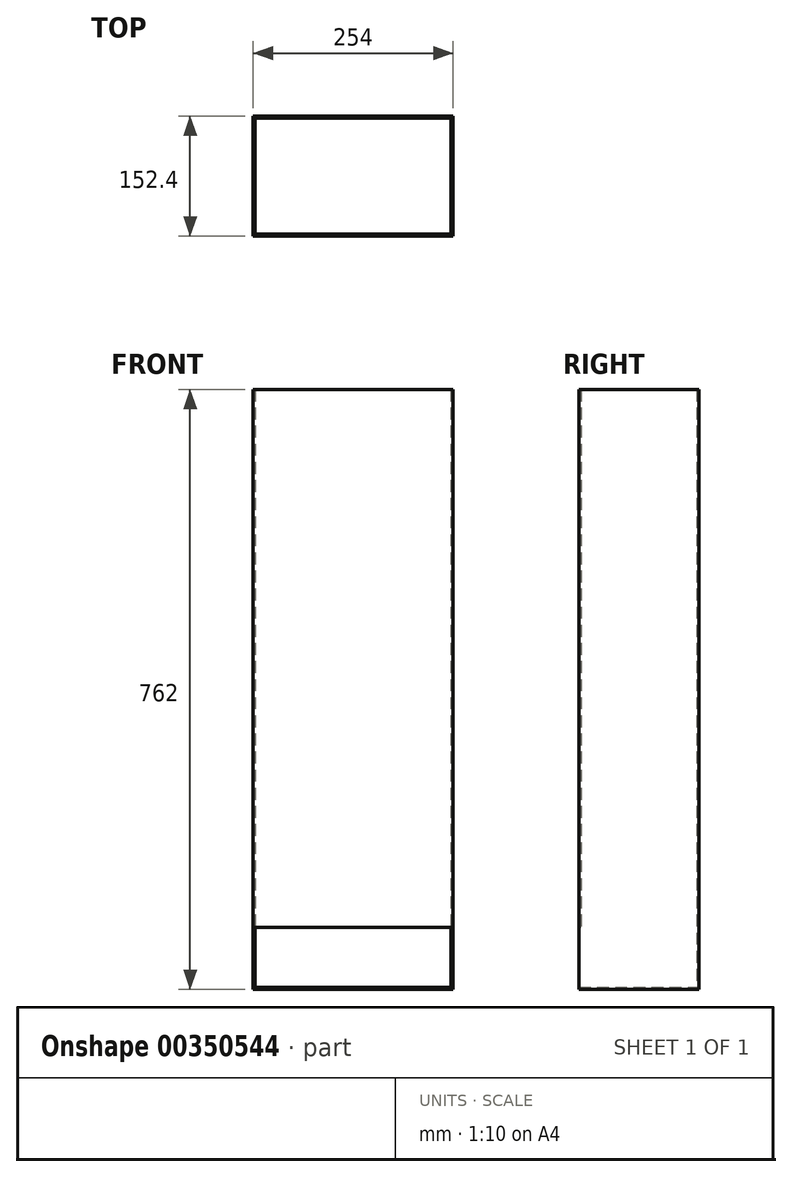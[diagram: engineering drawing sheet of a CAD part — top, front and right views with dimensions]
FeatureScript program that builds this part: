
annotation { "Feature Type Name" : "Feature", "Feature Type Description" : "" }
export const myFeature = defineFeature(function(context is Context, id is Id, definition is map)
    precondition{}
    {
        {
            var Q0;
            Q0=qCreatedBy(makeId("Front.planeOp"),FACE);
            var sketch = newSketch(context, id + "F0", { "sketchPlane" : qUnion([Q0])});
            skLineSegment(sketch, "E0.bottom", {"start": v(-266.83, 381.34) * mm, "end": v(-12.83, 381.34) * mm});
            skLineSegment(sketch, "E0.top", {"start": v(-266.83, -380.66) * mm, "end": v(-12.83, -380.66) * mm});
            skLineSegment(sketch, "E0.left", {"start": v(-266.83, 381.34) * mm, "end": v(-266.83, -380.66) * mm});
            skLineSegment(sketch, "E0.right", {"start": v(-12.83, 381.34) * mm, "end": v(-12.83, -380.66) * mm});
            skSolve(sketch);
        }
        {
            var Q0;
            Q0=makeQuery(id+"F0.imprint","IMPRINT",FACE,{"disambiguationData":[TD([[makeQuery(id+"F0.imprint","IMPRINT",EDGE,{"derivedFrom":sQuery(id+"F0.wireOp",EDGE,"E0.bottom")}),-1.0]])]});
            extrude(context, id + "F1", {"entities" : qUnion([Q0]), "depth" : 152.4 * mm});
        }
        {
            var Q0;
            Q0=makeQuery(id+"F1.opExtrude","CAP_FACE",FACE,{"disambiguationData":[OSD([sQuery(id+"F0.wireOp",EDGE,"E0.bottom"),sQuery(id+"F0.wireOp",EDGE,"E0.top"),sQuery(id+"F0.wireOp",EDGE,"E0.left"),sQuery(id+"F0.wireOp",EDGE,"E0.right")])],"isStart":false});
            var sketch = newSketch(context, id + "F2", { "sketchPlane" : qUnion([Q0])});
            skSolve(sketch);
        }
        {
            var Q0;
            Q0=makeQuery(id+"F1.opExtrude","SWEPT_FACE",FACE,{"disambiguationData":[OSD([sQuery(id+"F0.wireOp",EDGE,"E0.bottom")])]});
            shell(context, id + "F3", {"entities" : qUnion([Q0]), "thickness" : 2.54 * mm});
        }
        {
            var Q0;
            Q0=makeQuery(id+"F2.imprint","IMPRINT",FACE,{"disambiguationData":[TD([[makeQuery(id+"F2.imprint","IMPRINT",EDGE,{"derivedFrom":makeQuery(id+"F1.opExtrude","CAP_EDGE",EDGE,{"disambiguationData":[OSD([sQuery(id+"F0.wireOp",EDGE,"E0.bottom")])],"isStart":false})}),-1.0]])]});
            var sketch = newSketch(context, id + "F4", { "sketchPlane" : qUnion([Q0])});
            skLineSegment(sketch, "E1", {"start": v(-264.3, -378.12) * mm, "end": v(-264.3, -301.92) * mm});
            skLineSegment(sketch, "E2", {"start": v(-264.3, -301.92) * mm, "end": v(-15.37, -301.92) * mm});
            skLineSegment(sketch, "E3", {"start": v(-15.37, -301.92) * mm, "end": v(-15.37, -378.12) * mm});
            skLineSegment(sketch, "E4", {"start": v(-15.37, -378.12) * mm, "end": v(-264.3, -378.12) * mm});
            skSolve(sketch);
        }
        {
            var Q0;
            Q0=makeQuery(id+"F4.imprint","IMPRINT",FACE,{"disambiguationData":[TD([[makeQuery(id+"F4.imprint","IMPRINT",EDGE,{"derivedFrom":sQuery(id+"F4.wireOp",EDGE,"E1")}),-1.0]])]});
            extrude(context, id + "F5", {"entities" : qUnion([Q0]), "operationType" : NewBodyOperationType.REMOVE, "oppositeDirection" : true, "depth" : 12.7 * mm});
        }
    });
